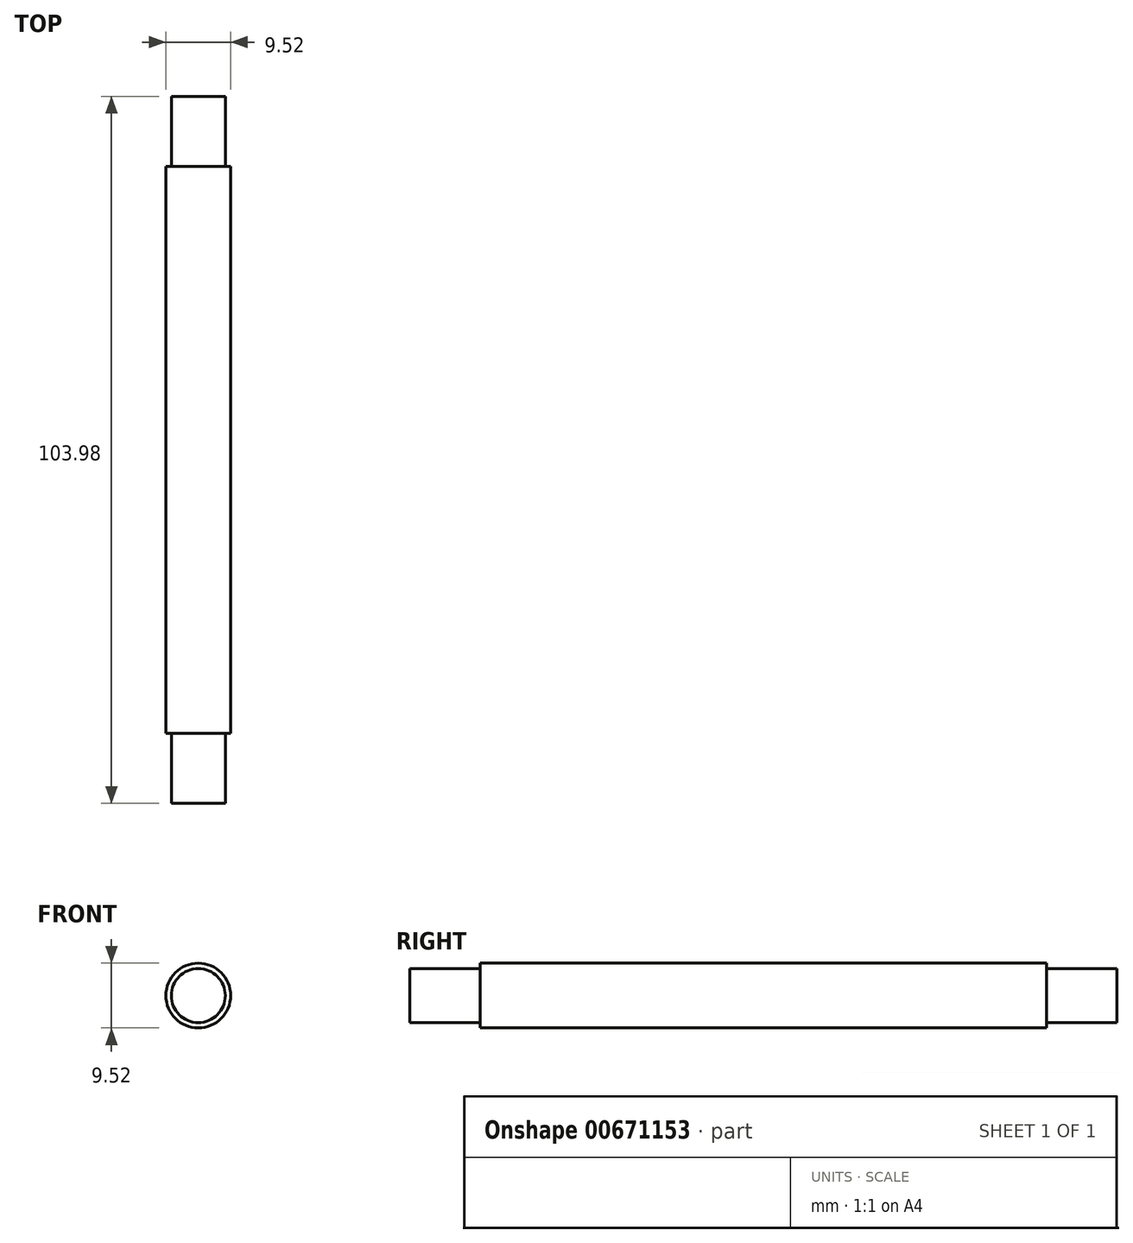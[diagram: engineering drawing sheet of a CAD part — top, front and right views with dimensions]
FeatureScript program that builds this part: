
annotation { "Feature Type Name" : "Feature", "Feature Type Description" : "" }
export const myFeature = defineFeature(function(context is Context, id is Id, definition is map)
    precondition{}
    {
        {
            var Q0;
            Q0=qCreatedBy(makeId("Front.planeOp"),FACE);
            var sketch = newSketch(context, id + "F0", { "sketchPlane" : qUnion([Q0])});
            skCircle(sketch, "E0", {"center": v(0, 0) * mm, "radius": 4.76 * mm});
            skSolve(sketch);
        }
        {
            var Q0;
            Q0=qSketchRegion(id+"F0",true);
            extrude(context, id + "F1", {"entities" : qUnion([Q0]), "depth" : 83.34 * mm});
        }
        {
            var Q0;
            Q0=makeQuery(id+"F1.opExtrude","CAP_FACE",FACE,{"disambiguationData":[OSD([sQuery(id+"F0.wireOp",EDGE,"E0")])],"isStart":false});
            var sketch = newSketch(context, id + "F2", { "sketchPlane" : qUnion([Q0])});
            skCircle(sketch, "E1", {"center": v(0, 0) * mm, "radius": 3.97 * mm});
            skSolve(sketch);
        }
        {
            var Q0;
            Q0=makeQuery(id+"F2.imprint","IMPRINT",FACE,{"disambiguationData":[TD([[makeQuery(id+"F2.imprint","IMPRINT",EDGE,{"derivedFrom":sQuery(id+"F2.wireOp",EDGE,"E1")}),1.0]])]});
            extrude(context, id + "F3", {"entities" : qUnion([Q0]), "operationType" : NewBodyOperationType.ADD, "depth" : 10.32 * mm});
        }
        {
            var Q0;
            Q0=makeQuery(id+"F1.opExtrude","CAP_FACE",FACE,{"disambiguationData":[OSD([sQuery(id+"F0.wireOp",EDGE,"E0")])],"isStart":true});
            var sketch = newSketch(context, id + "F4", { "sketchPlane" : qUnion([Q0])});
            skCircle(sketch, "E2", {"center": v(0, 0) * mm, "radius": 3.97 * mm});
            skSolve(sketch);
        }
        {
            var Q0;
            Q0=qSketchRegion(id+"F4",true);
            extrude(context, id + "F5", {"entities" : qUnion([Q0]), "operationType" : NewBodyOperationType.ADD, "depth" : 10.32 * mm});
        }
    });
